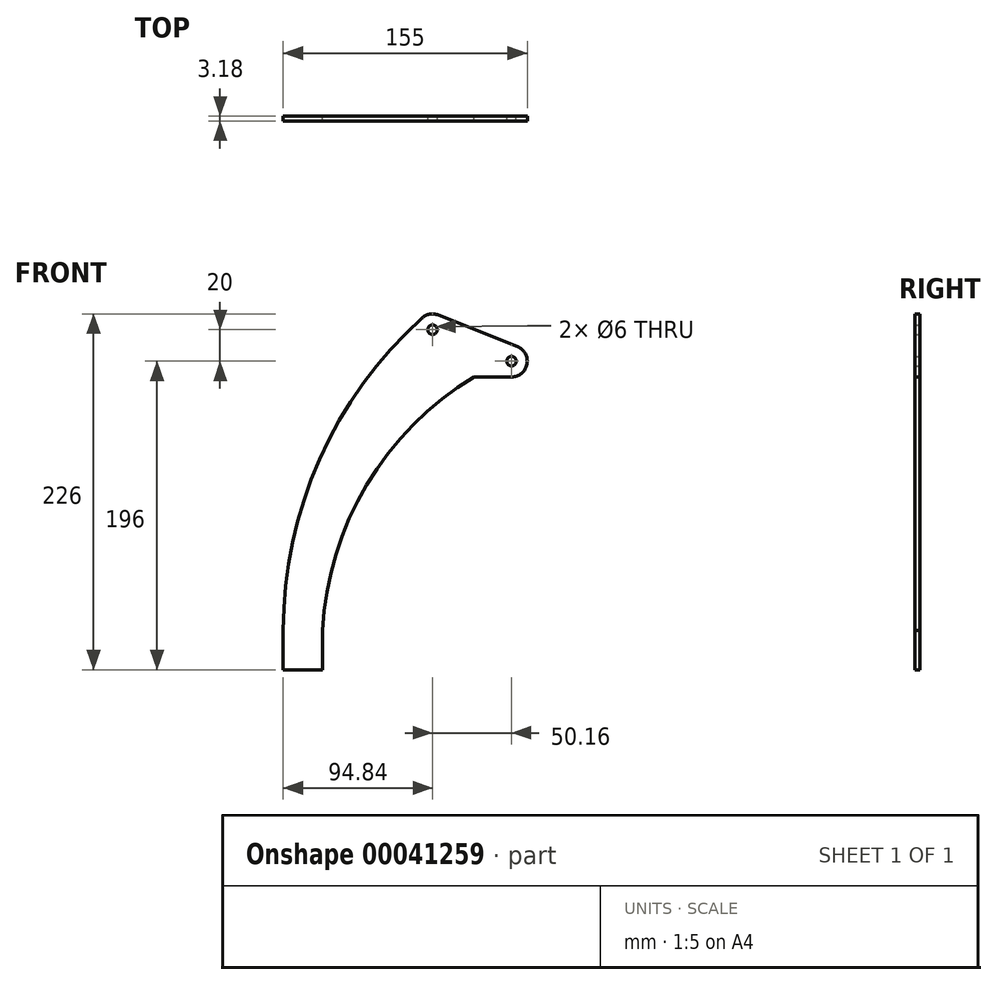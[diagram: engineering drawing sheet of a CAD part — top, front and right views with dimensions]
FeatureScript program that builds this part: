
annotation { "Feature Type Name" : "Feature", "Feature Type Description" : "" }
export const myFeature = defineFeature(function(context is Context, id is Id, definition is map)
    precondition{}
    {
        {
            var Q0;
            Q0=qCreatedBy(makeId("Front.planeOp"),FACE);
            var sketch = newSketch(context, id + "F0", { "sketchPlane" : qUnion([Q0])});
            skCircle(sketch, "E0", {"center": v(0, 0) * mm, "radius": 3 * mm});
            skArc(sketch, "E1", {"start": v(0, -10) * mm, "mid": v(9.82, -1.89) * mm, "end": v(3.7, 9.29) * mm});
            skCircle(sketch, "E2", {"center": v(-50.16, 20) * mm, "radius": 3 * mm});
            skLineSegment(sketch, "E3", {"start": v(-46.46, 29.29) * mm, "end": v(3.7, 9.29) * mm});
            skLineSegment(sketch, "E4", {"start": v(0, -10) * mm, "end": v(-23.83, -10) * mm});
            skArc(sketch, "E5", {"start": v(-23.83, -10) * mm, "mid": v(-91.96, -78.53) * mm, "end": v(-120, -171) * mm});
            skLineSegment(sketch, "E6", {"start": v(-120, -171) * mm, "end": v(-120, -196) * mm});
            skLineSegment(sketch, "E7", {"start": v(-120, -196) * mm, "end": v(-145, -196) * mm});
            skLineSegment(sketch, "E8", {"start": v(-145, -196) * mm, "end": v(-145, -171) * mm});
            skArc(sketch, "E9", {"start": v(-56.86, 27.42) * mm, "mid": v(-121.97, -62.44) * mm, "end": v(-145, -171) * mm});
            skArc(sketch, "E10", {"start": v(-46.46, 29.29) * mm, "mid": v(-51.93, 29.84) * mm, "end": v(-56.86, 27.42) * mm});
            skLineSegment(sketch, "E11", {"start": v(0, 0) * mm, "end": v(0, 48.02) * mm, "construction": true});
            skLineSegment(sketch, "E12", {"start": v(-50.16, 20) * mm, "end": v(-50.16, 48.3) * mm, "construction": true});
            skLineSegment(sketch, "E13", {"start": v(-50.16, 20) * mm, "end": v(-106.77, 20) * mm, "construction": true});
            skLineSegment(sketch, "E14", {"start": v(-145, -196) * mm, "end": v(-198.3, -196) * mm, "construction": true});
            skLineSegment(sketch, "E15", {"start": v(0, 0) * mm, "end": v(-58.68, 0) * mm, "construction": true});
            skSolve(sketch);
        }
        {
            var Q0;
            Q0=makeQuery(id+"F0.imprint","IMPRINT",FACE,{"disambiguationData":[TD([[makeQuery(id+"F0.imprint","IMPRINT",EDGE,{"derivedFrom":sQuery(id+"F0.wireOp",EDGE,"E0")}),-1.0]])]});
            extrude(context, id + "F1", {"entities" : qUnion([Q0]), "depth" : 3.17 * mm});
        }
    });
